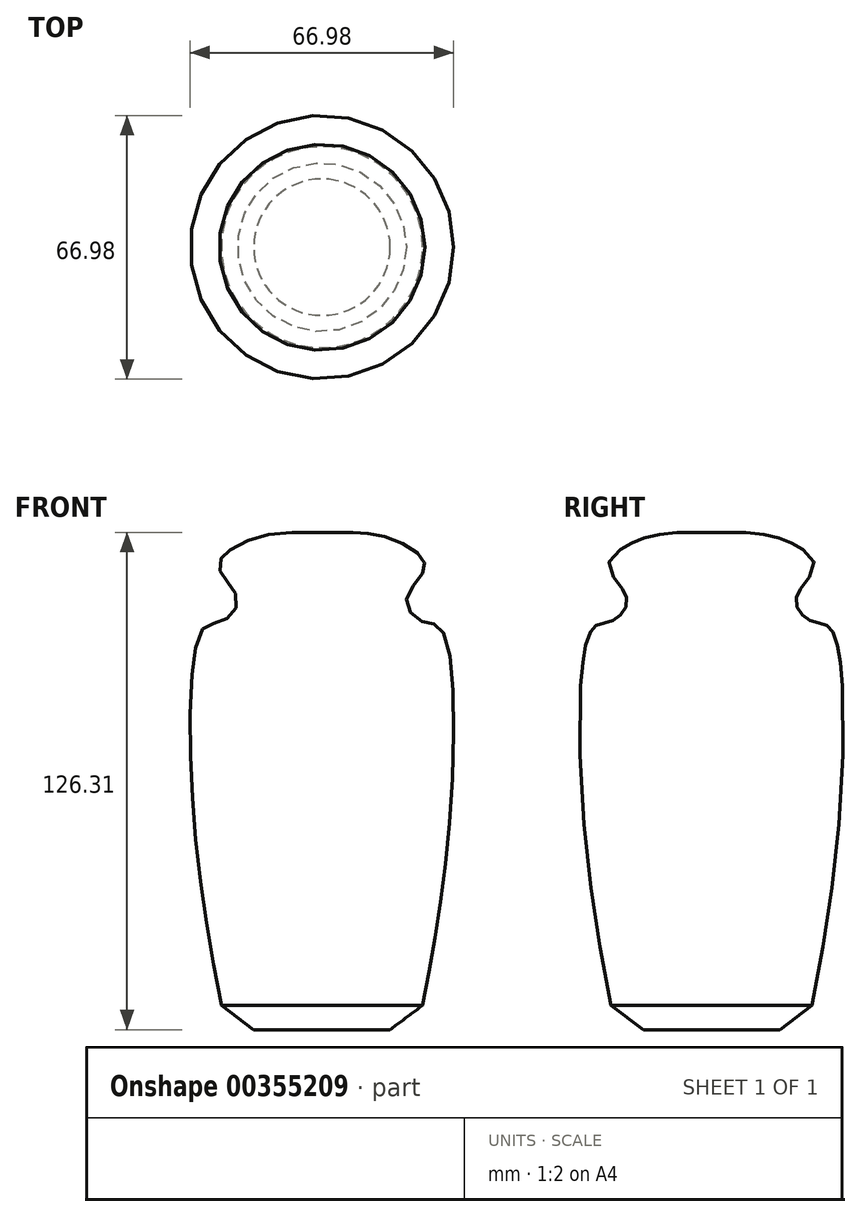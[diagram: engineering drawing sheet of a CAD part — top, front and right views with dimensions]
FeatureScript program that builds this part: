
annotation { "Feature Type Name" : "Feature", "Feature Type Description" : "" }
export const myFeature = defineFeature(function(context is Context, id is Id, definition is map)
    precondition{}
    {
        {
            var Q0;
            Q0=qCreatedBy(makeId("Front.planeOp"),FACE);
            var sketch = newSketch(context, id + "F0", { "sketchPlane" : qUnion([Q0])});
            skLineSegment(sketch, "E0", {"start": v(0, 61.09) * mm, "end": v(0, -70.78) * mm});
            skLineSegment(sketch, "E1", {"start": v(0, -58.15) * mm, "end": v(17.33, -58.15) * mm});
            skLineSegment(sketch, "E2", {"start": v(17.33, -58.15) * mm, "end": v(25.55, -51.98) * mm});
            skFitSpline(sketch, "E3", {"points": [v(25.55, -51.98) * mm, v(32.6, -3.23) * mm, v(30.25, 43.76) * mm, v(25.55, 45.52) * mm, v(21.44, 50.8) * mm, v(25.55, 57.86) * mm, v(25.55, 61.68) * mm, v(16.45, 66.96) * mm, v(7.34, 68.14) * mm, v(0, 68.14) * mm], "startDerivative": vector(38.98, 204.22) * mm, "endDerivative": vector(-86.83, -0.65) * mm});
            skLineSegment(sketch, "E4", {"start": v(0, 61.09) * mm, "end": v(0, 83.4) * mm});
            skSolve(sketch);
        }
        {
            var Q0;
            {var subQ1=sQuery(id+"F0.wireOp",EDGE,"E1");Q0=makeQuery(id+"F0.imprint","IMPRINT",FACE,{"disambiguationData":[TD([[makeQuery(id+"F0.imprint","IMPRINT",EDGE,{"derivedFrom":subQ1}),1.0]])]});}
            var Q1;
            Q1=sQuery(id+"F0.wireOp",EDGE,"E0");
            revolve(context, id + "F1", {"entities" : qUnion([Q0]), "axis" : qUnion([Q1]), "revolveType" : RevolveType.FULL});
        }
    });
